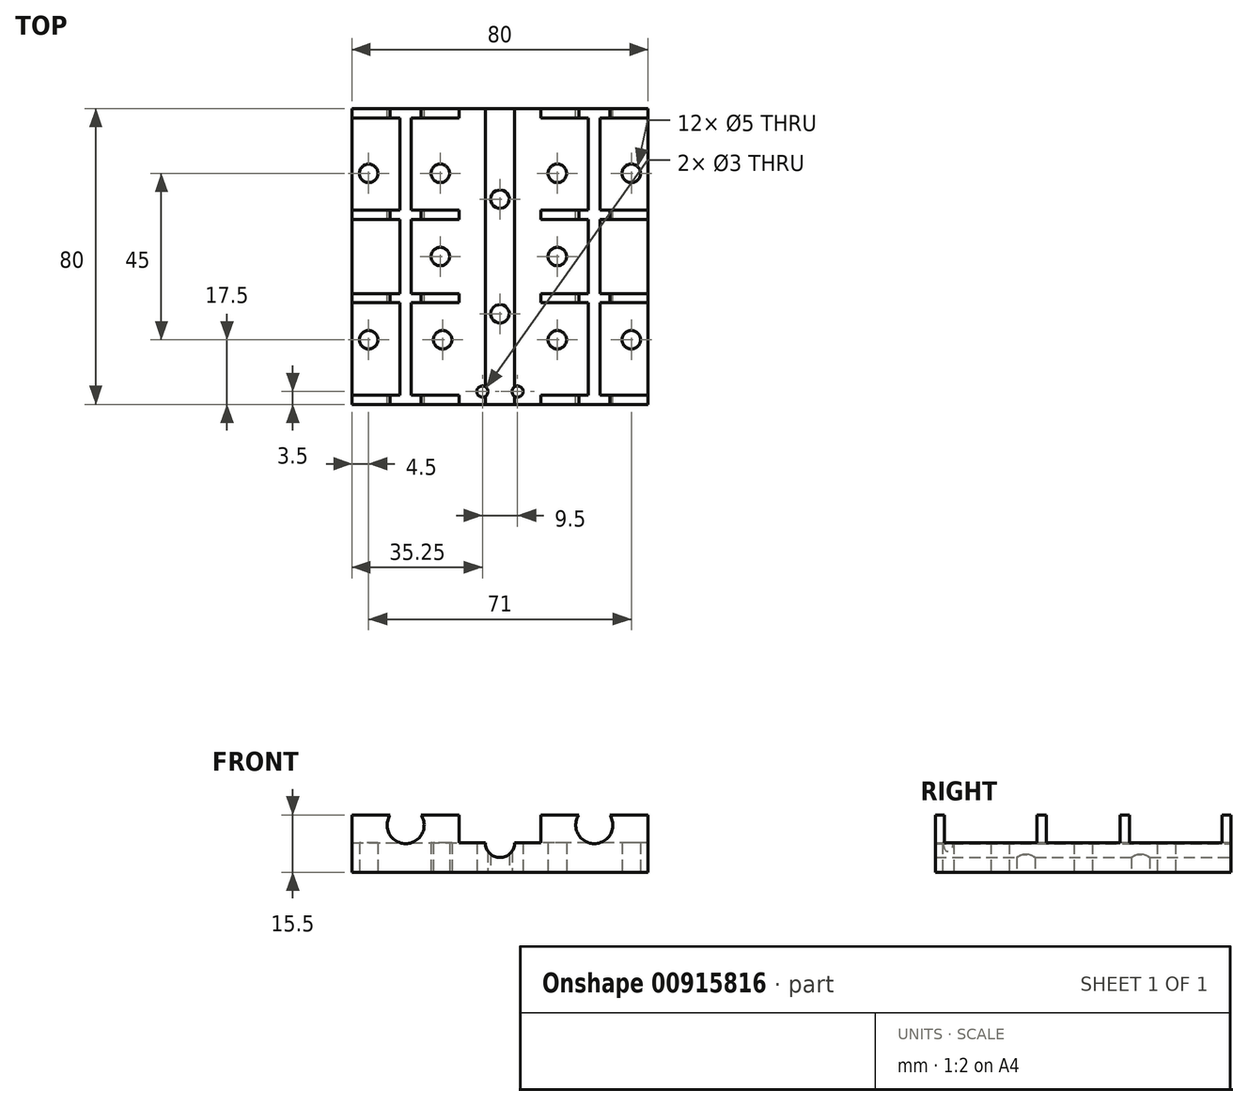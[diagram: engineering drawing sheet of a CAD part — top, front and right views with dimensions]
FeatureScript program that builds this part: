
annotation { "Feature Type Name" : "Feature", "Feature Type Description" : "" }
export const myFeature = defineFeature(function(context is Context, id is Id, definition is map)
    precondition{}
    {
        {
            var Q0;
            Q0=qCreatedBy(makeId("Top.planeOp"),FACE);
            var sketch = newSketch(context, id + "F0", { "sketchPlane" : qUnion([Q0])});
            skLineSegment(sketch, "E0.bottom", {"start": v(40, -40) * mm, "end": v(-40, -40) * mm});
            skLineSegment(sketch, "E0.top", {"start": v(40, 40) * mm, "end": v(-40, 40) * mm});
            skLineSegment(sketch, "E0.left", {"start": v(40, -40) * mm, "end": v(40, 40) * mm});
            skLineSegment(sketch, "E0.right", {"start": v(-40, -40) * mm, "end": v(-40, 40) * mm});
            skPoint(sketch, "E0.middle", {"position": v(0, 0) * mm});
            skCircle(sketch, "E1", {"center": v(-16.14, 22.5) * mm, "radius": 2.5 * mm});
            skCircle(sketch, "E2", {"center": v(35.5, 22.5) * mm, "radius": 2.5 * mm});
            skCircle(sketch, "E3", {"center": v(15.5, 22.5) * mm, "radius": 2.5 * mm});
            skCircle(sketch, "E4", {"center": v(-35.5, -22.5) * mm, "radius": 2.5 * mm});
            skCircle(sketch, "E5", {"center": v(-15.5, -22.5) * mm, "radius": 2.5 * mm});
            skCircle(sketch, "E6", {"center": v(35.5, -22.5) * mm, "radius": 2.5 * mm});
            skCircle(sketch, "E7", {"center": v(15.5, -22.5) * mm, "radius": 2.5 * mm});
            skCircle(sketch, "E8", {"center": v(-16.14, 0) * mm, "radius": 2.5 * mm});
            skCircle(sketch, "E9", {"center": v(0, -15.5) * mm, "radius": 2.5 * mm});
            skCircle(sketch, "E10", {"center": v(15.5, 0) * mm, "radius": 2.5 * mm});
            skCircle(sketch, "E11", {"center": v(0, 15.5) * mm, "radius": 2.5 * mm});
            skCircle(sketch, "E12", {"center": v(-35.5, 22.5) * mm, "radius": 2.5 * mm});
            skCircle(sketch, "E13", {"center": v(-4.75, -36.5) * mm, "radius": 1.5 * mm});
            skCircle(sketch, "E14", {"center": v(4.75, -36.5) * mm, "radius": 1.5 * mm});
            skSolve(sketch);
        }
        {
            var Q0;
            Q0 = qSketchRegion(id + "F0", true);
            extrude(context, id + "F1", {"entities" : qUnion([Q0]), "depth" : 8 * mm, "offsetDistance" : 25 * mm});
        }
        {
            var Q0;
            Q0=makeQuery(id+"F1.opExtrude","CAP_FACE",FACE,{"disambiguationData":[OSD([sQuery(id+"F0.wireOp",EDGE,"E0.bottom"),sQuery(id+"F0.wireOp",EDGE,"E0.top"),sQuery(id+"F0.wireOp",EDGE,"E0.left"),sQuery(id+"F0.wireOp",EDGE,"E0.right"),sQuery(id+"F0.wireOp",EDGE,"E1"),sQuery(id+"F0.wireOp",EDGE,"E2"),sQuery(id+"F0.wireOp",EDGE,"E3"),sQuery(id+"F0.wireOp",EDGE,"E4"),sQuery(id+"F0.wireOp",EDGE,"E5"),sQuery(id+"F0.wireOp",EDGE,"E6"),sQuery(id+"F0.wireOp",EDGE,"E7"),sQuery(id+"F0.wireOp",EDGE,"E8"),sQuery(id+"F0.wireOp",EDGE,"E9"),sQuery(id+"F0.wireOp",EDGE,"E10"),sQuery(id+"F0.wireOp",EDGE,"E11"),sQuery(id+"F0.wireOp",EDGE,"E12")])],"isStart":false});
            var sketch = newSketch(context, id + "F2", { "sketchPlane" : qUnion([Q0])});
            skLineSegment(sketch, "E15.bottom", {"start": v(-40, 40) * mm, "end": v(-11, 40) * mm});
            skLineSegment(sketch, "E15.top", {"start": v(-40, 37.5) * mm, "end": v(-11, 37.5) * mm});
            skLineSegment(sketch, "E15.left", {"start": v(-40, 40) * mm, "end": v(-40, 37.5) * mm});
            skLineSegment(sketch, "E15.right", {"start": v(-11, 40) * mm, "end": v(-11, 37.5) * mm});
            skLineSegment(sketch, "E16.bottom", {"start": v(40, 40) * mm, "end": v(11, 40) * mm});
            skLineSegment(sketch, "E16.top", {"start": v(40, 37.5) * mm, "end": v(11, 37.5) * mm});
            skLineSegment(sketch, "E16.left", {"start": v(40, 40) * mm, "end": v(40, 37.5) * mm});
            skLineSegment(sketch, "E16.right", {"start": v(11, 40) * mm, "end": v(11, 37.5) * mm});
            skLineSegment(sketch, "E17.bottom", {"start": v(-40, -40) * mm, "end": v(-11, -40) * mm});
            skLineSegment(sketch, "E17.top", {"start": v(-40, -37.5) * mm, "end": v(-11, -37.5) * mm});
            skLineSegment(sketch, "E17.left", {"start": v(-40, -40) * mm, "end": v(-40, -37.5) * mm});
            skLineSegment(sketch, "E17.right", {"start": v(-11, -40) * mm, "end": v(-11, -37.5) * mm});
            skLineSegment(sketch, "E18.bottom", {"start": v(40, -40) * mm, "end": v(11, -40) * mm});
            skLineSegment(sketch, "E18.top", {"start": v(40, -37.5) * mm, "end": v(11, -37.5) * mm});
            skLineSegment(sketch, "E18.left", {"start": v(40, -40) * mm, "end": v(40, -37.5) * mm});
            skLineSegment(sketch, "E18.right", {"start": v(11, -40) * mm, "end": v(11, -37.5) * mm});
            skLineSegment(sketch, "E19.bottom", {"start": v(-40, -10) * mm, "end": v(-11, -10) * mm});
            skLineSegment(sketch, "E19.top", {"start": v(-40, -12.5) * mm, "end": v(-11, -12.5) * mm});
            skLineSegment(sketch, "E19.left", {"start": v(-40, -10) * mm, "end": v(-40, -12.5) * mm});
            skLineSegment(sketch, "E19.right", {"start": v(-11, -10) * mm, "end": v(-11, -12.5) * mm});
            skLineSegment(sketch, "E20.bottom", {"start": v(11, -10) * mm, "end": v(40, -10) * mm});
            skLineSegment(sketch, "E20.top", {"start": v(11, -12.5) * mm, "end": v(40, -12.5) * mm});
            skLineSegment(sketch, "E20.left", {"start": v(11, -10) * mm, "end": v(11, -12.5) * mm});
            skLineSegment(sketch, "E20.right", {"start": v(40, -10) * mm, "end": v(40, -12.5) * mm});
            skLineSegment(sketch, "E21.bottom", {"start": v(-11, 12.5) * mm, "end": v(-40, 12.5) * mm});
            skLineSegment(sketch, "E21.top", {"start": v(-11, 10) * mm, "end": v(-40, 10) * mm});
            skLineSegment(sketch, "E21.left", {"start": v(-11, 12.5) * mm, "end": v(-11, 10) * mm});
            skLineSegment(sketch, "E21.right", {"start": v(-40, 12.5) * mm, "end": v(-40, 10) * mm});
            skLineSegment(sketch, "E22.bottom", {"start": v(11, 12.5) * mm, "end": v(40, 12.5) * mm});
            skLineSegment(sketch, "E22.top", {"start": v(11, 10) * mm, "end": v(40, 10) * mm});
            skLineSegment(sketch, "E22.left", {"start": v(11, 12.5) * mm, "end": v(11, 10) * mm});
            skLineSegment(sketch, "E22.right", {"start": v(40, 12.5) * mm, "end": v(40, 10) * mm});
            skSolve(sketch);
        }
        {
            var Q0;
            Q0 = qSketchRegion(id + "F2", true);
            extrude(context, id + "F3", {"entities" : qUnion([Q0]), "operationType" : NewBodyOperationType.ADD, "depth" : 7.5 * mm, "offsetDistance" : 25 * mm});
        }
        {
            var Q0;
            Q0=makeQuery(id+"F3.boolean.opBoolean","MERGE",FACE,{"derivedFrom":[makeQuery(id+"F1.opExtrude","SWEPT_FACE",FACE,{"disambiguationData":[OSD([sQuery(id+"F0.wireOp",EDGE,"E0.top")])]}),makeQuery(id+"F3.opExtrude","SWEPT_FACE",FACE,{"disambiguationData":[OSD([sQuery(id+"F2.wireOp",EDGE,"E15.bottom")])]}),makeQuery(id+"F3.opExtrude","SWEPT_FACE",FACE,{"disambiguationData":[OSD([sQuery(id+"F2.wireOp",EDGE,"E16.bottom")])]})]});
            var sketch = newSketch(context, id + "F4", { "sketchPlane" : qUnion([Q0])});
            skCircle(sketch, "E23", {"center": v(-25.5, 12.75) * mm, "radius": 5 * mm});
            skCircle(sketch, "E24", {"center": v(25.5, 12.75) * mm, "radius": 5 * mm});
            skCircle(sketch, "E25", {"center": v(0, 8) * mm, "radius": 4 * mm});
            skSolve(sketch);
        }
        {
            var Q0;
            Q0=sQuery(id+"F4.wireOp",VERTEX,"E23.center");
            var Q1;
            Q1=sQuery(id+"F4.wireOp",VERTEX,"E24.center");
            var Q2;
            Q2=makeQuery(id+"F1.opExtrude","SWEPT_BODY",BODY,{"disambiguationData":[OSD([sQuery(id+"F0.wireOp",EDGE,"E0.bottom"),sQuery(id+"F0.wireOp",EDGE,"E0.top"),sQuery(id+"F0.wireOp",EDGE,"E0.left"),sQuery(id+"F0.wireOp",EDGE,"E0.right"),sQuery(id+"F0.wireOp",EDGE,"E1"),sQuery(id+"F0.wireOp",EDGE,"E2"),sQuery(id+"F0.wireOp",EDGE,"E3"),sQuery(id+"F0.wireOp",EDGE,"E4"),sQuery(id+"F0.wireOp",EDGE,"E5"),sQuery(id+"F0.wireOp",EDGE,"E6"),sQuery(id+"F0.wireOp",EDGE,"E7"),sQuery(id+"F0.wireOp",EDGE,"E8"),sQuery(id+"F0.wireOp",EDGE,"E9"),sQuery(id+"F0.wireOp",EDGE,"E10"),sQuery(id+"F0.wireOp",EDGE,"E11"),sQuery(id+"F0.wireOp",EDGE,"E12")])]});
            hole(context, id + "F5", {"style" : HoleStyle.SIMPLE, "endStyle" : HoleEndStyle.THROUGH, "holeDiameter" : 10 * mm, "majorDiameter" : 5 * mm, "isTappedThrough" : true, "tappedDepth" : 12 * mm, "tapClearance" : 3, "locations" : qUnion([Q0, Q1]), "scope" : qUnion([Q2])});
        }
        {
            var Q0;
            Q0=makeQuery(id+"F3.boolean.opBoolean","MERGE",FACE,{"derivedFrom":[makeQuery(id+"F1.opExtrude","SWEPT_FACE",FACE,{"disambiguationData":[OSD([sQuery(id+"F0.wireOp",EDGE,"E0.top")])]}),makeQuery(id+"F3.opExtrude","SWEPT_FACE",FACE,{"disambiguationData":[OSD([sQuery(id+"F2.wireOp",EDGE,"E15.bottom")])]}),makeQuery(id+"F3.opExtrude","SWEPT_FACE",FACE,{"disambiguationData":[OSD([sQuery(id+"F2.wireOp",EDGE,"E16.bottom")])]})]});
            var sketch = newSketch(context, id + "F6", { "sketchPlane" : qUnion([Q0])});
            skCircle(sketch, "E26", {"center": v(0, 8) * mm, "radius": 4 * mm});
            skSolve(sketch);
        }
        {
            var Q0;
            Q0=sQuery(id+"F6.wireOp",VERTEX,"E26.center");
            var Q1;
            Q1=makeQuery(id+"F1.opExtrude","SWEPT_BODY",BODY,{"disambiguationData":[OSD([sQuery(id+"F0.wireOp",EDGE,"E0.bottom"),sQuery(id+"F0.wireOp",EDGE,"E0.top"),sQuery(id+"F0.wireOp",EDGE,"E0.left"),sQuery(id+"F0.wireOp",EDGE,"E0.right"),sQuery(id+"F0.wireOp",EDGE,"E1"),sQuery(id+"F0.wireOp",EDGE,"E2"),sQuery(id+"F0.wireOp",EDGE,"E3"),sQuery(id+"F0.wireOp",EDGE,"E4"),sQuery(id+"F0.wireOp",EDGE,"E5"),sQuery(id+"F0.wireOp",EDGE,"E6"),sQuery(id+"F0.wireOp",EDGE,"E7"),sQuery(id+"F0.wireOp",EDGE,"E8"),sQuery(id+"F0.wireOp",EDGE,"E9"),sQuery(id+"F0.wireOp",EDGE,"E10"),sQuery(id+"F0.wireOp",EDGE,"E11"),sQuery(id+"F0.wireOp",EDGE,"E12")])]});
            hole(context, id + "F7", {"style" : HoleStyle.SIMPLE, "endStyle" : HoleEndStyle.THROUGH, "holeDiameter" : 8 * mm, "majorDiameter" : 5 * mm, "isTappedThrough" : true, "tappedDepth" : 12 * mm, "tapClearance" : 3, "locations" : qUnion([Q0]), "scope" : qUnion([Q1])});
        }
    });
